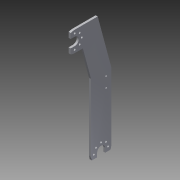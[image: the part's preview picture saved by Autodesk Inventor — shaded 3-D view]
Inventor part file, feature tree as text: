
AUTODESK INVENTOR PART (.ipt)
format: ipt  version: 2013 (Build 170138000, 138)  size: 199,680 bytes
history: native  units: mm
features: sketch x6, extrude x4, hole x2, pattern_circular x2, other x1
ambient origin geometry x8: Origin, YZ Plane, XZ Plane, XY Plane, X Axis, Y Axis, Z Axis, Center Point
feature tree (15):
  other  "ソリッド1"
  extrude  "押し出し1"  Depth=40.0mm
  extrude  "押し出し2"  Depth=20.0mm
  extrude  "押し出し3"  Depth=120.0mm
  hole  "穴1"  [1 undecoded]
  pattern_circular  "円形状パターン1"  [2 undecoded]
  pattern_circular  "円形状パターン2"  Count=2  [1 undecoded]
  hole  "穴2"  [1 undecoded]
  extrude  "押し出し4"  Depth=70.0mm
  sketch  "スケッチ1"
  sketch  "スケッチ2"
  sketch  "スケッチ3"
  sketch  "スケッチ4"
  sketch  "スケッチ5"
  sketch  "スケッチ6"
note: 5 required parameter values undecoded (feature->parameter linkage not recoverable at this tier; creation-order binding heuristic only, values carry confidence <= 0.55)
